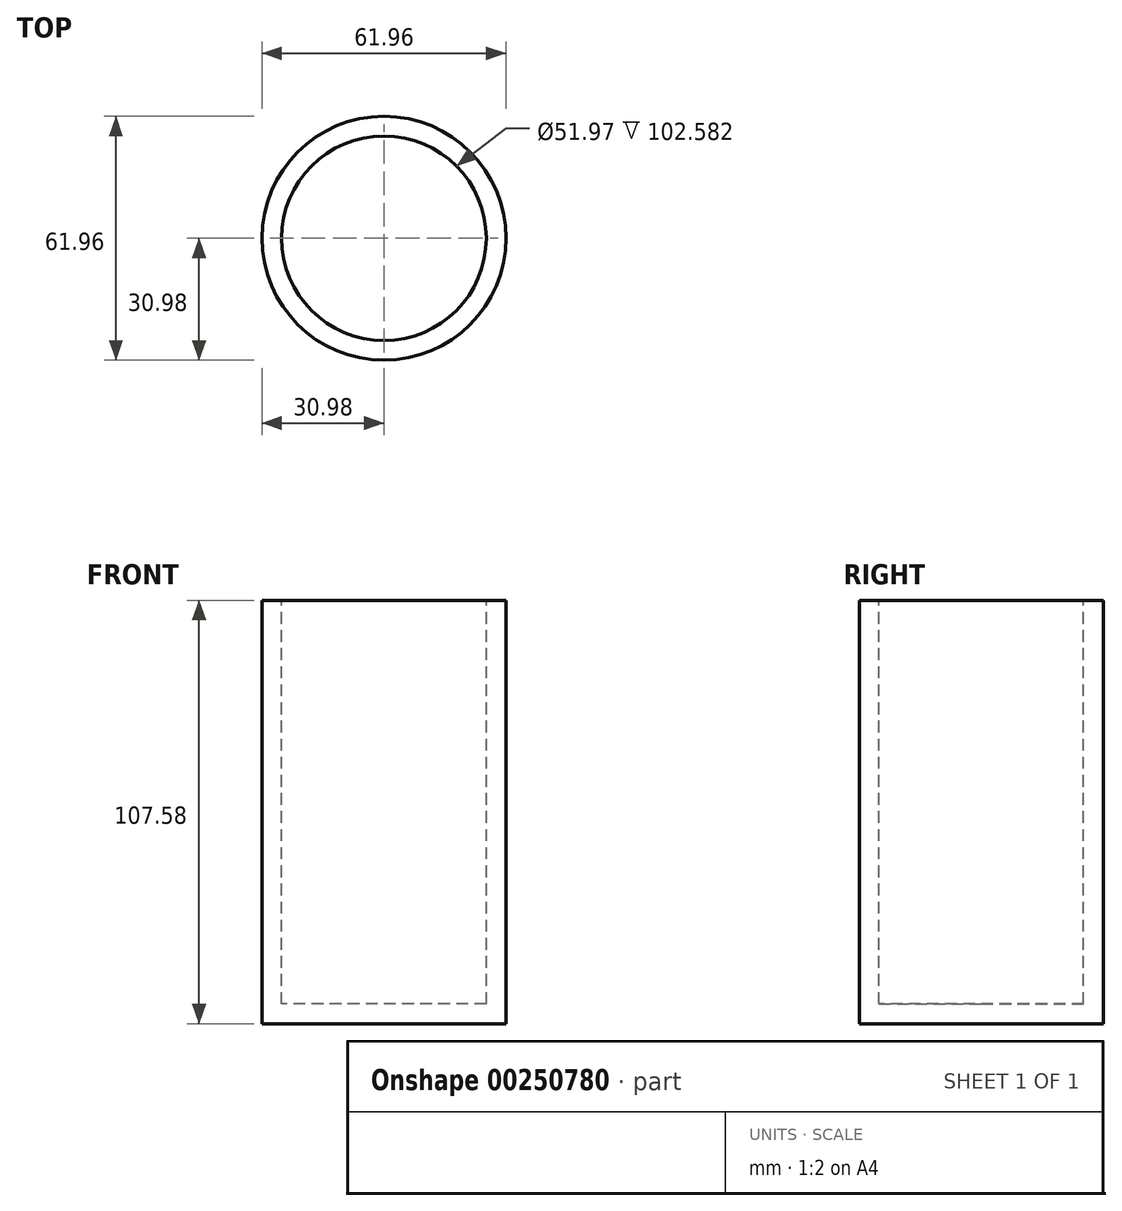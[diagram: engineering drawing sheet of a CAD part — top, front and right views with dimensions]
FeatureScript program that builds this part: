
annotation { "Feature Type Name" : "Feature", "Feature Type Description" : "" }
export const myFeature = defineFeature(function(context is Context, id is Id, definition is map)
    precondition{}
    {
        {
            var Q0;
            Q0=qCreatedBy(makeId("Front.planeOp"),FACE);
            var sketch = newSketch(context, id + "F0", { "sketchPlane" : qUnion([Q0])});
            skLineSegment(sketch, "E0.bottom", {"start": v(30.98, 53.8) * mm, "end": v(-30.98, 53.8) * mm});
            skLineSegment(sketch, "E0.top", {"start": v(30.98, -53.8) * mm, "end": v(-30.98, -53.8) * mm});
            skLineSegment(sketch, "E0.left", {"start": v(30.98, 53.8) * mm, "end": v(30.98, -53.8) * mm});
            skLineSegment(sketch, "E0.right", {"start": v(-30.98, 53.8) * mm, "end": v(-30.98, -53.8) * mm});
            skPoint(sketch, "E0.middle", {"position": v(0, 0) * mm});
            skLineSegment(sketch, "E1", {"start": v(0, 56.66) * mm, "end": v(0, -53.8) * mm});
            skPoint(sketch, "E1.startSnap0", {"position": v(0, 53.8) * mm});
            skSolve(sketch);
        }
        {
            var Q0;
            {var subQ0=sQuery(id+"F0.wireOp",EDGE,"E0.right");Q0=makeQuery(id+"F0.imprint","IMPRINT",FACE,{"disambiguationData":[TD([[makeQuery(id+"F0.imprint","IMPRINT",EDGE,{"derivedFrom":subQ0}),1.0]])]});}
            var Q1;
            Q1=sQuery(id+"F0.wireOp",EDGE,"E1");
            revolve(context, id + "F1", {"entities" : qUnion([Q0]), "axis" : qUnion([Q1]), "revolveType" : RevolveType.FULL});
        }
        {
            var Q0;
            Q0=makeQuery(id+"F1.opRevolve","SWEPT_FACE",FACE,{"disambiguationData":[OSD([sQuery(id+"F0.wireOp",EDGE,"E0.bottom")])]});
            shell(context, id + "F2", {"entities" : qUnion([Q0]), "thickness" : 5 * mm});
        }
    });
